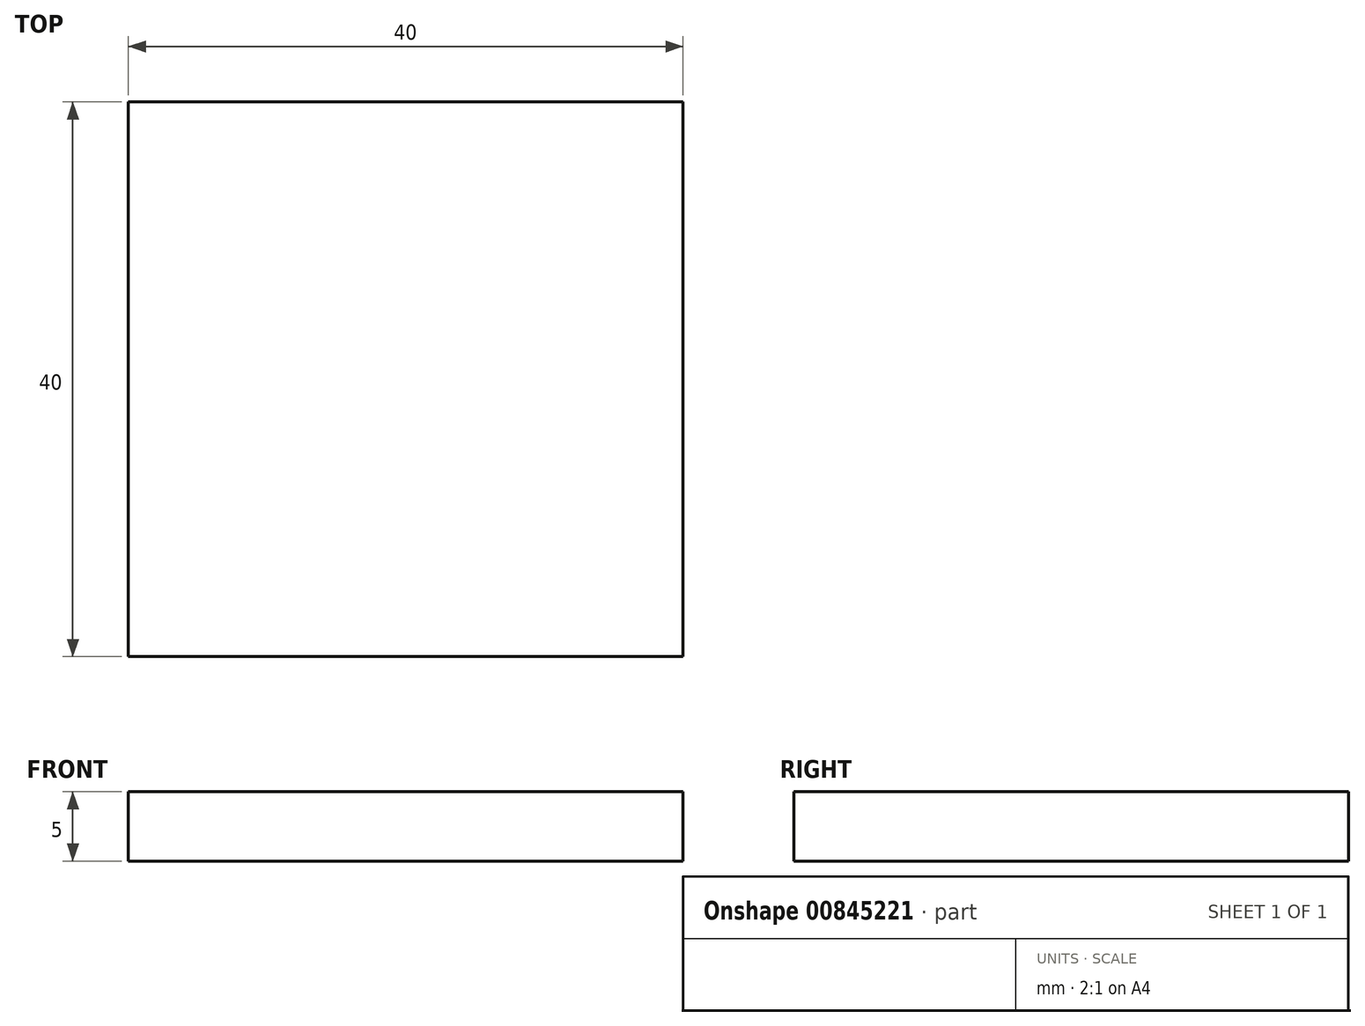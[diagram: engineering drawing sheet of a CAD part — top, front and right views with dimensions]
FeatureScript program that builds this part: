
annotation { "Feature Type Name" : "Feature", "Feature Type Description" : "" }
export const myFeature = defineFeature(function(context is Context, id is Id, definition is map)
    precondition{}
    {
        {
            var Q0;
            Q0=qCreatedBy(makeId("Top.planeOp"),FACE);
            var sketch = newSketch(context, id + "F0", { "sketchPlane" : qUnion([Q0])});
            skLineSegment(sketch, "E0.bottom", {"start": v(-18.84, 15.29) * mm, "end": v(21.16, 15.29) * mm});
            skLineSegment(sketch, "E0.top", {"start": v(-18.84, -24.71) * mm, "end": v(21.16, -24.71) * mm});
            skLineSegment(sketch, "E0.left", {"start": v(-18.84, 15.29) * mm, "end": v(-18.84, -24.71) * mm});
            skLineSegment(sketch, "E0.right", {"start": v(21.16, 15.29) * mm, "end": v(21.16, -24.71) * mm});
            skSolve(sketch);
        }
        {
            var Q0;
            Q0=makeQuery(id+"F0.imprint","IMPRINT",FACE,{"disambiguationData":[TD([[makeQuery(id+"F0.imprint","IMPRINT",EDGE,{"derivedFrom":sQuery(id+"F0.wireOp",EDGE,"E0.bottom")}),-1.0]])]});
            extrude(context, id + "F1", {"entities" : qUnion([Q0]), "depth" : 5 * mm, "offsetDistance" : 25 * mm});
        }
    });
